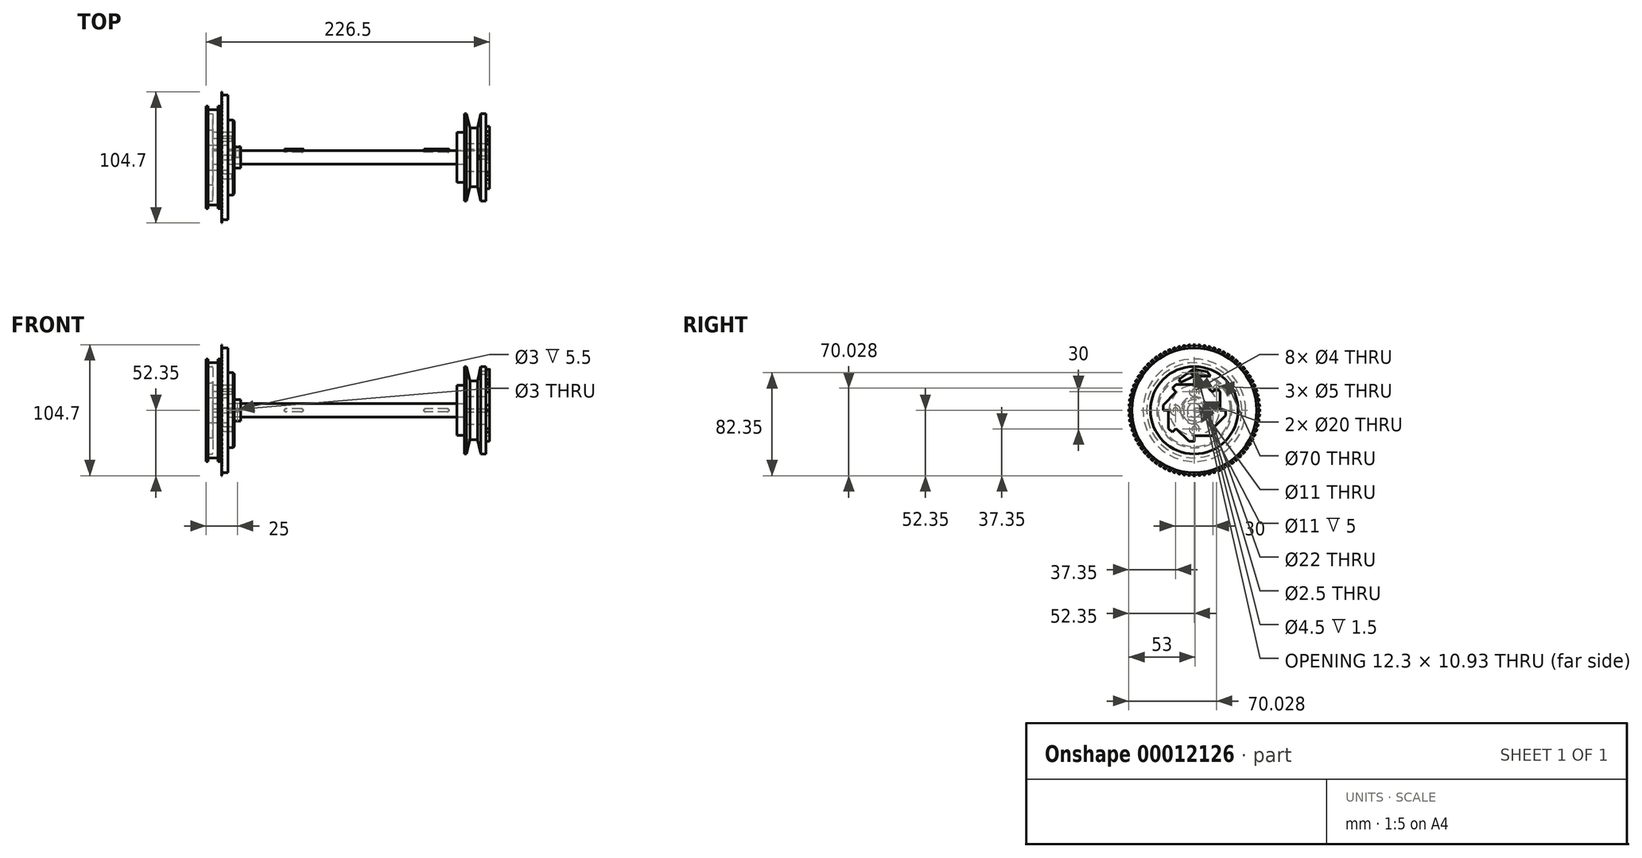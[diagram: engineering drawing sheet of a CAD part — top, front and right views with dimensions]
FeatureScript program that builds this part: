
annotation { "Feature Type Name" : "Feature", "Feature Type Description" : "" }
export const myFeature = defineFeature(function(context is Context, id is Id, definition is map)
    precondition{}
    {
        {
            var Q0;
            Q0=qCreatedBy(makeId("Right.planeOp"),FACE);
            var sketch = newSketch(context, id + "F0", { "sketchPlane" : qUnion([Q0])});
            skCircle(sketch, "E0", {"center": v(0, 0) * mm, "radius": 5.5 * mm});
            skSolve(sketch);
        }
        {
            var Q0;
            Q0=makeQuery(id+"F0.imprint","IMPRINT",FACE,{"disambiguationData":[TD([[makeQuery(id+"F0.imprint","IMPRINT",EDGE,{"derivedFrom":sQuery(id+"F0.wireOp",EDGE,"E0")}),1.0]])]});
            extrude(context, id + "F1", {"entities" : qUnion([Q0]), "depth" : 204 * mm, "symmetric" : true});
        }
        {
            var Q0;
            Q0=qCreatedBy(makeId("Front.planeOp"),FACE);
            cPlane(context, id + "F2", {"entities" : qUnion([Q0]), "cplaneType" : CPlaneType.OFFSET, "offset" : 5.5 * mm, "oppositeDirection" : true, "width" : 150 * mm, "height" : 150 * mm});
        }
        {
            var Q0;
            Q0=qCreatedBy(id+"F2.planeOp",FACE);
            var sketch = newSketch(context, id + "F3", { "sketchPlane" : qUnion([Q0])});
            skLineSegment(sketch, "E1.0", {"start": v(102, 5.5) * mm, "end": v(102, -5.5) * mm});
            skLineSegment(sketch, "E1.1", {"start": v(-102, 5.5) * mm, "end": v(-102, -5.5) * mm});
            skLineSegment(sketch, "E2", {"start": v(102, 0) * mm, "end": v(69.5, 0) * mm, "construction": true});
            skCircle(sketch, "E3", {"center": v(68.25, 0) * mm, "radius": 1.25 * mm});
            skCircle(sketch, "E4", {"center": v(50.75, 0) * mm, "radius": 1.25 * mm});
            skLineSegment(sketch, "E5", {"start": v(68.25, 1.25) * mm, "end": v(50.75, 1.25) * mm});
            skLineSegment(sketch, "E6", {"start": v(68.25, -1.25) * mm, "end": v(50.75, -1.25) * mm});
            skLineSegment(sketch, "E7", {"start": v(-102, 0) * mm, "end": v(-62, 0) * mm, "construction": true});
            skCircle(sketch, "E8", {"center": v(-60.75, 0) * mm, "radius": 1.25 * mm});
            skCircle(sketch, "E9", {"center": v(-48.25, 0) * mm, "radius": 1.25 * mm});
            skLineSegment(sketch, "E10", {"start": v(-48.25, 1.25) * mm, "end": v(-60.75, 1.25) * mm});
            skLineSegment(sketch, "E11", {"start": v(-48.25, -1.25) * mm, "end": v(-60.75, -1.25) * mm});
            skSolve(sketch);
        }
        {
            var Q0;
            {var subQ1=sQuery(id+"F3.wireOp",EDGE,"E5");Q0=makeQuery(id+"F3.imprint","IMPRINT",FACE,{"disambiguationData":[TD([[makeQuery(id+"F3.imprint","IMPRINT",EDGE,{"derivedFrom":subQ1}),1.0]])]});}
            var Q1;
            {var subQ0=sQuery(id+"F3.wireOp",EDGE,"E3");var subQ2=makeQuery(id+"F3.imprint","INTERSECT",VERTEX,{"derivedFrom":[subQ0,sQuery(id+"F3.wireOp",EDGE,"E5")]});Q1=makeQuery(id+"F3.imprint","IMPRINT",FACE,{"disambiguationData":[TD([[makeQuery(id+"F3.imprint","IMPRINT",EDGE,{"disambiguationData":[TD([[subQ2,-1.0]])],"derivedFrom":subQ0}),1.0]])]});}
            var Q2;
            {var subQ0=sQuery(id+"F3.wireOp",EDGE,"E4");var subQ2=makeQuery(id+"F3.imprint","INTERSECT",VERTEX,{"derivedFrom":[subQ0,sQuery(id+"F3.wireOp",EDGE,"E5")]});Q2=makeQuery(id+"F3.imprint","IMPRINT",FACE,{"disambiguationData":[TD([[makeQuery(id+"F3.imprint","IMPRINT",EDGE,{"disambiguationData":[TD([[subQ2,-1.0]])],"derivedFrom":subQ0}),1.0]])]});}
            var Q3;
            {var subQ0=sQuery(id+"F3.wireOp",EDGE,"E9");var subQ2=makeQuery(id+"F3.imprint","INTERSECT",VERTEX,{"derivedFrom":[subQ0,sQuery(id+"F3.wireOp",EDGE,"E10")]});Q3=makeQuery(id+"F3.imprint","IMPRINT",FACE,{"disambiguationData":[TD([[makeQuery(id+"F3.imprint","IMPRINT",EDGE,{"disambiguationData":[TD([[subQ2,-1.0]])],"derivedFrom":subQ0}),1.0]])]});}
            var Q4;
            {var subQ1=sQuery(id+"F3.wireOp",EDGE,"E10");Q4=makeQuery(id+"F3.imprint","IMPRINT",FACE,{"disambiguationData":[TD([[makeQuery(id+"F3.imprint","IMPRINT",EDGE,{"derivedFrom":subQ1}),1.0]])]});}
            var Q5;
            {var subQ0=sQuery(id+"F3.wireOp",EDGE,"E8");var subQ2=makeQuery(id+"F3.imprint","INTERSECT",VERTEX,{"derivedFrom":[subQ0,sQuery(id+"F3.wireOp",EDGE,"E10")]});Q5=makeQuery(id+"F3.imprint","IMPRINT",FACE,{"disambiguationData":[TD([[makeQuery(id+"F3.imprint","IMPRINT",EDGE,{"disambiguationData":[TD([[subQ2,-1.0]])],"derivedFrom":subQ0}),1.0]])]});}
            extrude(context, id + "F4", {"entities" : qUnion([Q0, Q1, Q2, Q3, Q4, Q5]), "operationType" : NewBodyOperationType.REMOVE, "depth" : 1.3 * mm});
        }
        {
            var Q0;
            {var subQ0=sQuery(id+"F3.wireOp",EDGE,"E3");var subQ2=makeQuery(id+"F3.imprint","INTERSECT",VERTEX,{"derivedFrom":[subQ0,sQuery(id+"F3.wireOp",EDGE,"E5")]});Q0=makeQuery(id+"F3.imprint","IMPRINT",FACE,{"disambiguationData":[TD([[makeQuery(id+"F3.imprint","IMPRINT",EDGE,{"disambiguationData":[TD([[subQ2,-1.0]])],"derivedFrom":subQ0}),1.0]])]});}
            var Q1;
            {var subQ1=sQuery(id+"F3.wireOp",EDGE,"E5");Q1=makeQuery(id+"F3.imprint","IMPRINT",FACE,{"disambiguationData":[TD([[makeQuery(id+"F3.imprint","IMPRINT",EDGE,{"derivedFrom":subQ1}),1.0]])]});}
            var Q2;
            {var subQ0=sQuery(id+"F3.wireOp",EDGE,"E4");var subQ2=makeQuery(id+"F3.imprint","INTERSECT",VERTEX,{"derivedFrom":[subQ0,sQuery(id+"F3.wireOp",EDGE,"E5")]});Q2=makeQuery(id+"F3.imprint","IMPRINT",FACE,{"disambiguationData":[TD([[makeQuery(id+"F3.imprint","IMPRINT",EDGE,{"disambiguationData":[TD([[subQ2,-1.0]])],"derivedFrom":subQ0}),1.0]])]});}
            var Q3;
            {var subQ0=sQuery(id+"F3.wireOp",EDGE,"E9");var subQ2=makeQuery(id+"F3.imprint","INTERSECT",VERTEX,{"derivedFrom":[subQ0,sQuery(id+"F3.wireOp",EDGE,"E10")]});Q3=makeQuery(id+"F3.imprint","IMPRINT",FACE,{"disambiguationData":[TD([[makeQuery(id+"F3.imprint","IMPRINT",EDGE,{"disambiguationData":[TD([[subQ2,-1.0]])],"derivedFrom":subQ0}),1.0]])]});}
            var Q4;
            {var subQ1=sQuery(id+"F3.wireOp",EDGE,"E10");Q4=makeQuery(id+"F3.imprint","IMPRINT",FACE,{"disambiguationData":[TD([[makeQuery(id+"F3.imprint","IMPRINT",EDGE,{"derivedFrom":subQ1}),1.0]])]});}
            var Q5;
            {var subQ0=sQuery(id+"F3.wireOp",EDGE,"E8");var subQ2=makeQuery(id+"F3.imprint","INTERSECT",VERTEX,{"derivedFrom":[subQ0,sQuery(id+"F3.wireOp",EDGE,"E10")]});Q5=makeQuery(id+"F3.imprint","IMPRINT",FACE,{"disambiguationData":[TD([[makeQuery(id+"F3.imprint","IMPRINT",EDGE,{"disambiguationData":[TD([[subQ2,-1.0]])],"derivedFrom":subQ0}),1.0]])]});}
            extrude(context, id + "F5", {"entities" : qUnion([Q0, Q1, Q2, Q3, Q4, Q5]), "depth" : 2.5 * mm, "symmetric" : true});
        }
        {
            var Q0;
            Q0=makeQuery(id+"F1.opExtrude","CAP_FACE",FACE,{"disambiguationData":[OSD([sQuery(id+"F0.wireOp",EDGE,"E0")])],"isStart":true});
            var sketch = newSketch(context, id + "F6", { "sketchPlane" : qUnion([Q0])});
            skCircle(sketch, "E12", {"center": v(0, 0) * mm, "radius": 10 * mm});
            skCircle(sketch, "E13", {"center": v(0, 0) * mm, "radius": 30 * mm});
            skLineSegment(sketch, "E14", {"start": v(0, 0) * mm, "end": v(0, -15) * mm, "construction": true});
            skLineSegment(sketch, "E15", {"start": v(0, 0) * mm, "end": v(-17.68, 17.68) * mm, "construction": true});
            skLineSegment(sketch, "E16", {"start": v(0, 0) * mm, "end": v(-5.5, 0) * mm, "construction": true});
            skCircle(sketch, "E17", {"center": v(0, -15) * mm, "radius": 2 * mm});
            skCircle(sketch, "E18", {"center": v(-17.68, 17.68) * mm, "radius": 2.5 * mm});
            skLineSegment(sketch, "E19.rect.bottom", {"start": v(-6.8, -1.25) * mm, "end": v(-4.2, -1.25) * mm});
            skLineSegment(sketch, "E19.rect.top", {"start": v(-6.8, 1.25) * mm, "end": v(-4.2, 1.25) * mm});
            skLineSegment(sketch, "E19.rect.left", {"start": v(-6.8, -1.25) * mm, "end": v(-6.8, 1.25) * mm});
            skLineSegment(sketch, "E19.rect.right", {"start": v(-4.2, -1.25) * mm, "end": v(-4.2, 1.25) * mm});
            skPoint(sketch, "E19.rect.middle", {"position": v(-5.5, 0) * mm});
            skCircle(sketch, "E20.1.0", {"center": v(15, 0) * mm, "radius": 2 * mm});
            skCircle(sketch, "E20.2.0", {"center": v(0, 15) * mm, "radius": 2 * mm});
            skCircle(sketch, "E20.3.0", {"center": v(-15, 0) * mm, "radius": 2 * mm});
            skSolve(sketch);
        }
        {
            var Q0;
            Q0=makeQuery(id+"F6.imprint","IMPRINT",FACE,{"disambiguationData":[TD([[makeQuery(id+"F6.imprint","IMPRINT",EDGE,{"derivedFrom":sQuery(id+"F6.wireOp",EDGE,"E12")}),-1.0]])]});
            extrude(context, id + "F7", {"entities" : qUnion([Q0]), "depth" : 5 * mm});
        }
        {
            var Q0;
            Q0=makeQuery(id+"F6.imprint","IMPRINT",FACE,{"disambiguationData":[TD([[makeQuery(id+"F6.imprint","IMPRINT",EDGE,{"derivedFrom":sQuery(id+"F6.wireOp",EDGE,"E12")}),1.0]])]});
            extrude(context, id + "F8", {"entities" : qUnion([Q0]), "operationType" : NewBodyOperationType.ADD, "depth" : 17 * mm});
        }
        {
            var Q0;
            Q0=makeQuery(id+"F7.opExtrude","CAP_EDGE",EDGE,{"disambiguationData":[OSD([sQuery(id+"F6.wireOp",EDGE,"E13")])],"isStart":true});
            chamfer(context, id + "F9", {"entities" : qUnion([Q0]), "width" : 1 * mm, "tangentPropagation" : true});
        }
        {
            var Q0;
            Q0=makeQuery(id+"F7.opExtrude","CAP_EDGE",EDGE,{"disambiguationData":[OSD([sQuery(id+"F6.wireOp",EDGE,"E20.1.0")])],"isStart":true});
            var Q1;
            Q1=makeQuery(id+"F7.opExtrude","CAP_EDGE",EDGE,{"disambiguationData":[OSD([sQuery(id+"F6.wireOp",EDGE,"E17")])],"isStart":true});
            var Q2;
            Q2=makeQuery(id+"F7.opExtrude","CAP_EDGE",EDGE,{"disambiguationData":[OSD([sQuery(id+"F6.wireOp",EDGE,"E20.3.0")])],"isStart":true});
            var Q3;
            Q3=makeQuery(id+"F7.opExtrude","CAP_EDGE",EDGE,{"disambiguationData":[OSD([sQuery(id+"F6.wireOp",EDGE,"E20.2.0")])],"isStart":true});
            chamfer(context, id + "F10", {"entities" : qUnion([Q0, Q1, Q2, Q3]), "width" : 2 * mm, "tangentPropagation" : true});
        }
        {
            var Q0;
            Q0=makeQuery(id+"F1.opExtrude","CAP_FACE",FACE,{"disambiguationData":[OSD([sQuery(id+"F0.wireOp",EDGE,"E0")])],"isStart":false});
            var sketch = newSketch(context, id + "F11", { "sketchPlane" : qUnion([Q0])});
            skLineSegment(sketch, "E21.0", {"start": v(4.25, 1.25) * mm, "end": v(6.75, 1.25) * mm});
            skLineSegment(sketch, "E21.1", {"start": v(4.25, -1.25) * mm, "end": v(6.75, -1.25) * mm});
            skCircle(sketch, "E22", {"center": v(0, 0) * mm, "radius": 11 * mm});
            skCircle(sketch, "E23", {"center": v(0, 0) * mm, "radius": 20.5 * mm});
            skCircle(sketch, "E24", {"center": v(0, 0) * mm, "radius": 25.25 * mm});
            skLineSegment(sketch, "E25", {"start": v(0, 0) * mm, "end": v(5.5, 0) * mm, "construction": true});
            skLineSegment(sketch, "E26.rect.bottom", {"start": v(6.8, -1.25) * mm, "end": v(4.2, -1.25) * mm});
            skLineSegment(sketch, "E26.rect.top", {"start": v(6.8, 1.25) * mm, "end": v(4.2, 1.25) * mm});
            skLineSegment(sketch, "E26.rect.left", {"start": v(6.8, -1.25) * mm, "end": v(6.8, 1.25) * mm});
            skLineSegment(sketch, "E26.rect.right", {"start": v(4.2, -1.25) * mm, "end": v(4.2, 1.25) * mm});
            skPoint(sketch, "E26.rect.middle", {"position": v(5.5, 0) * mm});
            skLineSegment(sketch, "E27", {"start": v(20.5, 0) * mm, "end": v(25.25, 0) * mm});
            skLineSegment(sketch, "E28.1.0", {"start": v(14.5, 14.5) * mm, "end": v(17.85, 17.85) * mm});
            skLineSegment(sketch, "E28.2.0", {"start": v(0, 20.5) * mm, "end": v(0, 25.25) * mm});
            skLineSegment(sketch, "E28.3.0", {"start": v(-14.5, 14.5) * mm, "end": v(-17.85, 17.85) * mm});
            skLineSegment(sketch, "E28.4.0", {"start": v(-20.5, 0) * mm, "end": v(-25.25, 0) * mm});
            skLineSegment(sketch, "E28.5.0", {"start": v(-14.5, -14.5) * mm, "end": v(-17.85, -17.85) * mm});
            skLineSegment(sketch, "E28.6.0", {"start": v(0, -20.5) * mm, "end": v(0, -25.25) * mm});
            skLineSegment(sketch, "E28.7.0", {"start": v(14.5, -14.5) * mm, "end": v(17.85, -17.85) * mm});
            skLineSegment(sketch, "E29", {"start": v(0, -20.5) * mm, "end": v(14.74, -20.5) * mm});
            skLineSegment(sketch, "E30", {"start": v(14.74, -20.5) * mm, "end": v(17.62, -17.62) * mm});
            skLineSegment(sketch, "E31.1.0", {"start": v(14.5, -14.5) * mm, "end": v(24.92, -4.07) * mm});
            skLineSegment(sketch, "E31.1.1", {"start": v(24.92, -4.07) * mm, "end": v(24.92, 0) * mm});
            skLineSegment(sketch, "E31.2.0", {"start": v(20.5, 0) * mm, "end": v(20.5, 14.74) * mm});
            skLineSegment(sketch, "E31.2.1", {"start": v(20.5, 14.74) * mm, "end": v(17.62, 17.62) * mm});
            skLineSegment(sketch, "E31.3.0", {"start": v(14.5, 14.5) * mm, "end": v(4.07, 24.92) * mm});
            skLineSegment(sketch, "E31.3.1", {"start": v(4.07, 24.92) * mm, "end": v(0, 24.92) * mm});
            skLineSegment(sketch, "E31.4.0", {"start": v(0, 20.5) * mm, "end": v(-14.74, 20.5) * mm});
            skLineSegment(sketch, "E31.4.1", {"start": v(-14.74, 20.5) * mm, "end": v(-17.62, 17.62) * mm});
            skLineSegment(sketch, "E31.5.0", {"start": v(-14.5, 14.5) * mm, "end": v(-24.92, 4.07) * mm});
            skLineSegment(sketch, "E31.5.1", {"start": v(-24.92, 4.07) * mm, "end": v(-24.92, 0) * mm});
            skLineSegment(sketch, "E31.6.0", {"start": v(-20.5, 0) * mm, "end": v(-20.5, -14.74) * mm});
            skLineSegment(sketch, "E31.6.1", {"start": v(-20.5, -14.74) * mm, "end": v(-17.62, -17.62) * mm});
            skLineSegment(sketch, "E31.7.0", {"start": v(-14.5, -14.5) * mm, "end": v(-4.07, -24.92) * mm});
            skLineSegment(sketch, "E31.7.1", {"start": v(-4.07, -24.92) * mm, "end": v(0, -24.92) * mm});
            skSolve(sketch);
        }
        {
            var Q0;
            {var subQ1=sQuery(id+"F11.wireOp",EDGE,"E31.5.0");Q0=makeQuery(id+"F11.imprint","IMPRINT",FACE,{"disambiguationData":[TD([[makeQuery(id+"F11.imprint","IMPRINT",EDGE,{"derivedFrom":subQ1}),1.0]])]});}
            var Q1;
            {var subQ1=sQuery(id+"F11.wireOp",EDGE,"E31.4.0");Q1=makeQuery(id+"F11.imprint","IMPRINT",FACE,{"disambiguationData":[TD([[makeQuery(id+"F11.imprint","IMPRINT",EDGE,{"derivedFrom":subQ1}),1.0]])]});}
            var Q2;
            {var subQ1=sQuery(id+"F11.wireOp",EDGE,"E31.3.0");Q2=makeQuery(id+"F11.imprint","IMPRINT",FACE,{"disambiguationData":[TD([[makeQuery(id+"F11.imprint","IMPRINT",EDGE,{"derivedFrom":subQ1}),1.0]])]});}
            var Q3;
            {var subQ1=sQuery(id+"F11.wireOp",EDGE,"E31.2.0");Q3=makeQuery(id+"F11.imprint","IMPRINT",FACE,{"disambiguationData":[TD([[makeQuery(id+"F11.imprint","IMPRINT",EDGE,{"derivedFrom":subQ1}),1.0]])]});}
            var Q4;
            {var subQ1=sQuery(id+"F11.wireOp",EDGE,"E31.1.0");Q4=makeQuery(id+"F11.imprint","IMPRINT",FACE,{"disambiguationData":[TD([[makeQuery(id+"F11.imprint","IMPRINT",EDGE,{"derivedFrom":subQ1}),1.0]])]});}
            var Q5;
            {var subQ1=sQuery(id+"F11.wireOp",EDGE,"E29");Q5=makeQuery(id+"F11.imprint","IMPRINT",FACE,{"disambiguationData":[TD([[makeQuery(id+"F11.imprint","IMPRINT",EDGE,{"derivedFrom":subQ1}),1.0]])]});}
            var Q6;
            {var subQ1=sQuery(id+"F11.wireOp",EDGE,"E31.7.0");Q6=makeQuery(id+"F11.imprint","IMPRINT",FACE,{"disambiguationData":[TD([[makeQuery(id+"F11.imprint","IMPRINT",EDGE,{"derivedFrom":subQ1}),1.0]])]});}
            var Q7;
            {var subQ1=sQuery(id+"F11.wireOp",EDGE,"E31.6.0");Q7=makeQuery(id+"F11.imprint","IMPRINT",FACE,{"disambiguationData":[TD([[makeQuery(id+"F11.imprint","IMPRINT",EDGE,{"derivedFrom":subQ1}),1.0]])]});}
            var Q8;
            Q8=makeQuery(id+"F11.imprint","IMPRINT",FACE,{"disambiguationData":[TD([[makeQuery(id+"F11.imprint","IMPRINT",EDGE,{"derivedFrom":sQuery(id+"F11.wireOp",EDGE,"E22")}),-1.0]])]});
            extrude(context, id + "F12", {"entities" : qUnion([Q0, Q1, Q2, Q3, Q4, Q5, Q6, Q7, Q8]), "oppositeDirection" : true, "depth" : 3 * mm});
        }
        {
            var Q0;
            Q0=makeQuery(id+"F11.imprint","IMPRINT",FACE,{"disambiguationData":[TD([[makeQuery(id+"F11.imprint","IMPRINT",EDGE,{"derivedFrom":sQuery(id+"F11.wireOp",EDGE,"E22")}),1.0]])]});
            extrude(context, id + "F13", {"entities" : qUnion([Q0]), "operationType" : NewBodyOperationType.ADD, "oppositeDirection" : true, "depth" : 20 * mm});
        }
        {
            var Q0;
            Q0=makeQuery(id+"F7.opExtrude","CAP_FACE",FACE,{"disambiguationData":[OSD([sQuery(id+"F6.wireOp",EDGE,"E12"),sQuery(id+"F6.wireOp",EDGE,"E13"),sQuery(id+"F6.wireOp",EDGE,"E17"),sQuery(id+"F6.wireOp",EDGE,"E18"),sQuery(id+"F6.wireOp",EDGE,"E20.1.0"),sQuery(id+"F6.wireOp",EDGE,"E20.2.0"),sQuery(id+"F6.wireOp",EDGE,"E20.3.0")])],"isStart":false});
            var sketch = newSketch(context, id + "F14", { "sketchPlane" : qUnion([Q0])});
            skCircle(sketch, "E32", {"center": v(0, 0) * mm, "radius": 52.35 * mm});
            skCircle(sketch, "E33", {"center": v(0, 0) * mm, "radius": 51.1 * mm, "construction": true});
            skCircle(sketch, "E34", {"center": v(0, 0) * mm, "radius": 49.85 * mm});
            skLineSegment(sketch, "E35", {"start": v(0, 0) * mm, "end": v(0, 52.35) * mm, "construction": true});
            skLineSegment(sketch, "E36", {"start": v(0, 49.85) * mm, "end": v(15, 49.85) * mm, "construction": true});
            skLineSegment(sketch, "E37", {"start": v(0, 0) * mm, "end": v(-1, 51.1) * mm, "construction": true});
            skLineSegment(sketch, "E38", {"start": v(0, 0) * mm, "end": v(-3.15, 49.75) * mm, "construction": true});
            skArc(sketch, "E39", {"start": v(-0.86, 52.34) * mm, "mid": v(-1, 51.1) * mm, "end": v(-1.05, 49.84) * mm});
            skArc(sketch, "E40.0.MirrorCS", {"start": v(0.86, 52.34) * mm, "mid": v(1, 51.1) * mm, "end": v(1.05, 49.84) * mm});
            skSolve(sketch);
        }
        {
            var Q0;
            Q0=makeQuery(id+"F14.imprint","IMPRINT",FACE,{"disambiguationData":[TD([[makeQuery(id+"F14.imprint","IMPRINT",EDGE,{"derivedFrom":makeQuery(id+"F7.opExtrude","CAP_EDGE",EDGE,{"disambiguationData":[OSD([sQuery(id+"F6.wireOp",EDGE,"E13")])],"isStart":false})}),-1.0]])]});
            var Q1;
            {var subQ1=sQuery(id+"F14.wireOp",EDGE,"E39");Q1=makeQuery(id+"F14.imprint","IMPRINT",FACE,{"disambiguationData":[TD([[makeQuery(id+"F14.imprint","IMPRINT",EDGE,{"derivedFrom":subQ1}),1.0]])]});}
            var Q2;
            Q2=makeQuery(id+"F14.imprint","IMPRINT",FACE,{"disambiguationData":[TD([[makeQuery(id+"F14.imprint","IMPRINT",EDGE,{"derivedFrom":makeQuery(id+"F7.opExtrude","CAP_EDGE",EDGE,{"disambiguationData":[OSD([sQuery(id+"F6.wireOp",EDGE,"E13")])],"isStart":false})}),1.0]])]});
            extrude(context, id + "F15", {"entities" : qUnion([Q0, Q1, Q2]), "depth" : 5 * mm});
        }
        {
            var Q0;
            Q0=makeQuery(id+"F15.opExtrude","SWEPT_FACE",FACE,{"disambiguationData":[OSD([sQuery(id+"F14.wireOp",EDGE,"E40.0.MirrorCS")])]});
            var Q1;
            Q1=makeQuery(id+"F15.opExtrude","SWEPT_FACE",FACE,{"disambiguationData":[OSD([sQuery(id+"F14.wireOp",EDGE,"E32")])]});
            var Q2;
            Q2=makeQuery(id+"F15.opExtrude","SWEPT_FACE",FACE,{"disambiguationData":[OSD([sQuery(id+"F14.wireOp",EDGE,"E39")])]});
            var Q3;
            Q3=makeQuery(id+"F8.opExtrude","CAP_EDGE",EDGE,{"disambiguationData":[OSD([sQuery(id+"F6.wireOp",EDGE,"E12")])],"isStart":false});
            circularPattern(context, id + "F16", {"faces" : qUnion([Q0, Q1, Q2]), "axis" : qUnion([Q3]), "angle" : 4.5 * degree, "instanceCount" : round(80), "patternType" : PatternType.FACE, "computeTransformsWithoutBuiltin" : true});
        }
        {
            var Q0;
            Q0=qCreatedBy(makeId("Front.planeOp"),FACE);
            var sketch = newSketch(context, id + "F17", { "sketchPlane" : qUnion([Q0])});
            skLineSegment(sketch, "E41.0", {"start": v(-107, -30) * mm, "end": v(-107, 30) * mm});
            skLineSegment(sketch, "E42", {"start": v(-107, 0) * mm, "end": v(-134.37, 0) * mm, "construction": true});
            skLineSegment(sketch, "E43", {"start": v(-107, 0) * mm, "end": v(-107, 49.85) * mm, "construction": true});
            skLineSegment(sketch, "E44.bottom", {"start": v(-107, 49.85) * mm, "end": v(-112, 49.85) * mm});
            skLineSegment(sketch, "E44.top", {"start": v(-107, 52.35) * mm, "end": v(-112, 52.35) * mm});
            skLineSegment(sketch, "E44.left", {"start": v(-107, 49.85) * mm, "end": v(-107, 52.35) * mm});
            skLineSegment(sketch, "E44.right", {"start": v(-112, 49.85) * mm, "end": v(-112, 52.35) * mm});
            skLineSegment(sketch, "E45", {"start": v(-109.5, 52.35) * mm, "end": v(-109.5, 49.85) * mm, "construction": true});
            skLineSegment(sketch, "E46", {"start": v(-107, 49.85) * mm, "end": v(-117, 49.85) * mm, "construction": true});
            skLineSegment(sketch, "E47", {"start": v(-107, 51.1) * mm, "end": v(-112, 51.1) * mm, "construction": true});
            skArc(sketch, "E48", {"start": v(-107, 51.1) * mm, "mid": v(-107.1, 51.73) * mm, "end": v(-107.24, 52.35) * mm});
            skArc(sketch, "E49.0.MirrorCS", {"start": v(-112, 51.1) * mm, "mid": v(-111.9, 51.73) * mm, "end": v(-111.76, 52.35) * mm});
            skSolve(sketch);
        }
        {
            var Q0;
            {var subQ0=sQuery(id+"F17.wireOp",EDGE,"E49.0.MirrorCS");Q0=makeQuery(id+"F17.imprint","IMPRINT",FACE,{"disambiguationData":[TD([[makeQuery(id+"F17.imprint","IMPRINT",EDGE,{"derivedFrom":subQ0}),1.0]])]});}
            var Q1;
            {var subQ0=sQuery(id+"F17.wireOp",EDGE,"E48");Q1=makeQuery(id+"F17.imprint","IMPRINT",FACE,{"disambiguationData":[TD([[makeQuery(id+"F17.imprint","IMPRINT",EDGE,{"derivedFrom":subQ0}),-1.0]])]});}
            var Q2;
            Q2=sQuery(id+"F17.wireOp",EDGE,"E42");
            revolve(context, id + "F18", {"operationType" : NewBodyOperationType.REMOVE, "entities" : qUnion([Q0, Q1]), "axis" : qUnion([Q2]), "revolveType" : RevolveType.FULL, "oppositeDirection" : true});
        }
        {
            var Q0;
            Q0=qCreatedBy(makeId("Front.planeOp"),FACE);
            var sketch = newSketch(context, id + "F19", { "sketchPlane" : qUnion([Q0])});
            skLineSegment(sketch, "E50.0", {"start": v(-112, -10) * mm, "end": v(-112, 10) * mm});
            skLineSegment(sketch, "E51", {"start": v(-112, 0) * mm, "end": v(-131.3, 0) * mm, "construction": true});
            skLineSegment(sketch, "E52", {"start": v(-112, 10) * mm, "end": v(-112, 22) * mm});
            skLineSegment(sketch, "E53", {"start": v(-112, 22) * mm, "end": v(-113.5, 22) * mm});
            skLineSegment(sketch, "E54", {"start": v(-113.5, 22) * mm, "end": v(-113.5, 41) * mm});
            skLineSegment(sketch, "E55", {"start": v(-113.5, 41) * mm, "end": v(-115, 41) * mm});
            skLineSegment(sketch, "E56", {"start": v(-115, 41) * mm, "end": v(-115, 38) * mm});
            skLineSegment(sketch, "E57", {"start": v(-115, 38) * mm, "end": v(-123, 38) * mm});
            skLineSegment(sketch, "E58", {"start": v(-123, 38) * mm, "end": v(-123, 41) * mm});
            skLineSegment(sketch, "E59", {"start": v(-123, 41) * mm, "end": v(-124.5, 41) * mm});
            skLineSegment(sketch, "E60", {"start": v(-124.5, 41) * mm, "end": v(-124.5, 35) * mm});
            skLineSegment(sketch, "E61", {"start": v(-124.5, 35) * mm, "end": v(-119, 35) * mm});
            skLineSegment(sketch, "E62", {"start": v(-119, 35) * mm, "end": v(-119, 22) * mm});
            skLineSegment(sketch, "E63", {"start": v(-119, 22) * mm, "end": v(-124.5, 22) * mm});
            skLineSegment(sketch, "E64", {"start": v(-124.5, 22) * mm, "end": v(-124.5, 10) * mm});
            skLineSegment(sketch, "E65", {"start": v(-124.5, 10) * mm, "end": v(-112, 10) * mm});
            skSolve(sketch);
        }
        {
            var Q0;
            Q0=makeQuery(id+"F19.imprint","IMPRINT",FACE,{"disambiguationData":[TD([[makeQuery(id+"F19.imprint","IMPRINT",EDGE,{"derivedFrom":sQuery(id+"F19.wireOp",EDGE,"E52")}),1.0]])]});
            var Q1;
            Q1=sQuery(id+"F19.wireOp",EDGE,"E51");
            revolve(context, id + "F20", {"entities" : qUnion([Q0]), "axis" : qUnion([Q1]), "revolveType" : RevolveType.FULL});
        }
        {
            var Q0;
            Q0=makeQuery(id+"F20.opRevolve","SWEPT_EDGE",EDGE,{"disambiguationData":[OSD([sQuery(id+"F19.wireOp",EDGE,"E53"),sQuery(id+"F19.wireOp",EDGE,"E54")])]});
            var Q1;
            Q1=makeQuery(id+"F20.opRevolve","SWEPT_EDGE",EDGE,{"disambiguationData":[OSD([sQuery(id+"F19.wireOp",EDGE,"E62"),sQuery(id+"F19.wireOp",EDGE,"E63")])]});
            var Q2;
            Q2=makeQuery(id+"F20.opRevolve","SWEPT_EDGE",EDGE,{"disambiguationData":[OSD([sQuery(id+"F19.wireOp",EDGE,"E61"),sQuery(id+"F19.wireOp",EDGE,"E62")])]});
            var Q3;
            Q3=makeQuery(id+"F20.opRevolve","SWEPT_EDGE",EDGE,{"disambiguationData":[OSD([sQuery(id+"F19.wireOp",EDGE,"E63"),sQuery(id+"F19.wireOp",EDGE,"E64")])]});
            var Q4;
            Q4=makeQuery(id+"F20.opRevolve","SWEPT_EDGE",EDGE,{"disambiguationData":[OSD([sQuery(id+"F19.wireOp",EDGE,"E60"),sQuery(id+"F19.wireOp",EDGE,"E61")])]});
            fillet(context, id + "F21", {"entities" : qUnion([Q0, Q1, Q2, Q3, Q4]), "radius" : 1 * mm, "tangentPropagation" : true, "allowEdgeOverflow" : false});
        }
        {
            var Q0;
            Q0=makeQuery(id+"F20.opRevolve","SWEPT_FACE",FACE,{"disambiguationData":[OSD([sQuery(id+"F19.wireOp",EDGE,"E54")])]});
            var sketch = newSketch(context, id + "F22", { "sketchPlane" : qUnion([Q0])});
            skCircle(sketch, "E66.0", {"center": v(17.68, 17.68) * mm, "radius": 2.5 * mm});
            skSolve(sketch);
        }
        {
            var Q0;
            {var subQ0=sQuery(id+"F19.wireOp",EDGE,"E54");var subQ1=makeQuery(id+"F21.opFillet","BLEND_EDGE",EDGE,{"blendedFrom":[makeQuery(id+"F20.opRevolve","SWEPT_EDGE",EDGE,{"disambiguationData":[OSD([sQuery(id+"F19.wireOp",EDGE,"E53"),subQ0])]}),makeQuery(id+"F20.opRevolve","SWEPT_FACE",FACE,{"disambiguationData":[OSD([subQ0])]})],"blendedInto":[makeQuery(id+"F20.opRevolve","SWEPT_FACE",FACE,{"disambiguationData":[OSD([subQ0])]})]});var subQ2=sQuery(id+"F22.wireOp",EDGE,"E66.0");var subQ4=makeQuery(id+"F22.imprint","INTERSECT",VERTEX,{"disambiguationData":[OD(0.0)],"derivedFrom":[subQ1,subQ2]});Q0=makeQuery(id+"F22.imprint","IMPRINT",FACE,{"disambiguationData":[TD([[makeQuery(id+"F22.imprint","IMPRINT",EDGE,{"disambiguationData":[TD([[subQ4,1.0]])],"derivedFrom":subQ2}),1.0]])]});}
            var Q1;
            {var subQ0=sQuery(id+"F19.wireOp",EDGE,"E54");var subQ1=makeQuery(id+"F21.opFillet","BLEND_EDGE",EDGE,{"blendedFrom":[makeQuery(id+"F20.opRevolve","SWEPT_EDGE",EDGE,{"disambiguationData":[OSD([sQuery(id+"F19.wireOp",EDGE,"E53"),subQ0])]}),makeQuery(id+"F20.opRevolve","SWEPT_FACE",FACE,{"disambiguationData":[OSD([subQ0])]})],"blendedInto":[makeQuery(id+"F20.opRevolve","SWEPT_FACE",FACE,{"disambiguationData":[OSD([subQ0])]})]});var subQ2=sQuery(id+"F22.wireOp",EDGE,"E66.0");var subQ4=makeQuery(id+"F22.imprint","INTERSECT",VERTEX,{"disambiguationData":[OD(0.0)],"derivedFrom":[subQ1,subQ2]});Q1=makeQuery(id+"F22.imprint","IMPRINT",FACE,{"disambiguationData":[TD([[makeQuery(id+"F22.imprint","IMPRINT",EDGE,{"disambiguationData":[TD([[subQ4,-1.0]])],"derivedFrom":subQ2}),1.0]])]});}
            extrude(context, id + "F23", {"entities" : qUnion([Q0, Q1]), "operationType" : NewBodyOperationType.REMOVE, "oppositeDirection" : true, "depth" : 13 * mm, "symmetric" : true});
        }
        {
            var Q0;
            Q0=qCreatedBy(makeId("Front.planeOp"),FACE);
            var sketch = newSketch(context, id + "F24", { "sketchPlane" : qUnion([Q0])});
            skLineSegment(sketch, "E67.0", {"start": v(82, 11) * mm, "end": v(82, -11) * mm});
            skLineSegment(sketch, "E67.1", {"start": v(99, 11) * mm, "end": v(99, -11) * mm});
            skLineSegment(sketch, "E68", {"start": v(99, 0) * mm, "end": v(82, 0) * mm, "construction": true});
            skLineSegment(sketch, "E69", {"start": v(99, 11) * mm, "end": v(99, 35) * mm});
            skLineSegment(sketch, "E70", {"start": v(99, 35) * mm, "end": v(95, 35) * mm});
            skLineSegment(sketch, "E71", {"start": v(95, 35) * mm, "end": v(92.25, 23.5) * mm});
            skLineSegment(sketch, "E72", {"start": v(92.25, 23.5) * mm, "end": v(86.25, 23.5) * mm});
            skLineSegment(sketch, "E73", {"start": v(86.25, 23.5) * mm, "end": v(83.5, 35) * mm});
            skLineSegment(sketch, "E74", {"start": v(83.5, 35) * mm, "end": v(82, 35) * mm});
            skLineSegment(sketch, "E75", {"start": v(82, 35) * mm, "end": v(82, 11) * mm});
            skLineSegment(sketch, "E76", {"start": v(82, 11) * mm, "end": v(99, 11) * mm});
            skSolve(sketch);
        }
        {
            var Q0;
            Q0=makeQuery(id+"F24.imprint","IMPRINT",FACE,{"disambiguationData":[TD([[makeQuery(id+"F24.imprint","IMPRINT",EDGE,{"derivedFrom":sQuery(id+"F24.wireOp",EDGE,"E69")}),1.0]])]});
            var Q1;
            Q1=sQuery(id+"F24.wireOp",EDGE,"E68");
            revolve(context, id + "F25", {"entities" : qUnion([Q0]), "axis" : qUnion([Q1]), "revolveType" : RevolveType.FULL});
        }
        {
            var Q0;
            Q0=makeQuery(id+"F25.opRevolve","SWEPT_FACE",FACE,{"disambiguationData":[OSD([sQuery(id+"F24.wireOp",EDGE,"E69")])]});
            var sketch = newSketch(context, id + "F26", { "sketchPlane" : qUnion([Q0])});
            skLineSegment(sketch, "E77", {"start": v(0, 0) * mm, "end": v(0, 30) * mm, "construction": true});
            skCircle(sketch, "E78", {"center": v(0, 30) * mm, "radius": 1.25 * mm});
            skSolve(sketch);
        }
        {
            var Q0;
            Q0=makeQuery(id+"F26.imprint","IMPRINT",FACE,{"disambiguationData":[TD([[makeQuery(id+"F26.imprint","IMPRINT",EDGE,{"derivedFrom":sQuery(id+"F26.wireOp",EDGE,"E78")}),1.0]])]});
            extrude(context, id + "F27", {"entities" : qUnion([Q0]), "operationType" : NewBodyOperationType.REMOVE, "oppositeDirection" : true, "depth" : 8 * mm});
        }
        {
            var Q0;
            Q0=makeQuery(id+"F25.opRevolve","SWEPT_FACE",FACE,{"disambiguationData":[OSD([sQuery(id+"F24.wireOp",EDGE,"E75")])]});
            var sketch = newSketch(context, id + "F28", { "sketchPlane" : qUnion([Q0])});
            skCircle(sketch, "E79.0", {"center": v(0, 0) * mm, "radius": 23.5 * mm});
            skLineSegment(sketch, "E80", {"start": v(0, 0) * mm, "end": v(0, -23.5) * mm, "construction": true});
            skCircle(sketch, "E81", {"center": v(0, -24.25) * mm, "radius": 0.75 * mm});
            skSolve(sketch);
        }
        {
            var Q0;
            Q0=makeQuery(id+"F28.imprint","IMPRINT",FACE,{"disambiguationData":[TD([[makeQuery(id+"F28.imprint","IMPRINT",EDGE,{"derivedFrom":sQuery(id+"F28.wireOp",EDGE,"E81")}),1.0]])]});
            extrude(context, id + "F29", {"entities" : qUnion([Q0]), "operationType" : NewBodyOperationType.REMOVE, "oppositeDirection" : true, "depth" : 8 * mm});
        }
        {
            var Q0;
            Q0=makeQuery(id+"F13.opExtrude","CAP_FACE",FACE,{"disambiguationData":[OSD([sQuery(id+"F0.wireOp",EDGE,"E0"),sQuery(id+"F11.wireOp",EDGE,"E22"),sQuery(id+"F11.wireOp",EDGE,"E26.rect.bottom"),sQuery(id+"F11.wireOp",EDGE,"E26.rect.top"),sQuery(id+"F11.wireOp",EDGE,"E26.rect.left")])],"isStart":false});
            var sketch = newSketch(context, id + "F30", { "sketchPlane" : qUnion([Q0])});
            skCircle(sketch, "E82.0", {"center": v(0, 0) * mm, "radius": 5.5 * mm});
            skCircle(sketch, "E83", {"center": v(0, 0) * mm, "radius": 20 * mm});
            skSolve(sketch);
        }
        {
            var Q0;
            Q0=makeQuery(id+"F30.imprint","IMPRINT",FACE,{"disambiguationData":[TD([[makeQuery(id+"F30.imprint","IMPRINT",EDGE,{"derivedFrom":sQuery(id+"F30.wireOp",EDGE,"E83")}),1.0]])]});
            var Q1;
            Q1=makeQuery(id+"F30.imprint","IMPRINT",FACE,{"disambiguationData":[TD([[makeQuery(id+"F30.imprint","IMPRINT",EDGE,{"disambiguationData":[OD(0.0)],"derivedFrom":sQuery(id+"F30.wireOp",EDGE,"E82.0")}),1.0]])]});
            var Q2;
            Q2=makeQuery(id+"F30.imprint","IMPRINT",FACE,{"disambiguationData":[TD([[makeQuery(id+"F30.imprint","IMPRINT",EDGE,{"disambiguationData":[OD(1.0)],"derivedFrom":sQuery(id+"F30.wireOp",EDGE,"E82.0")}),-1.0]])]});
            extrude(context, id + "F31", {"entities" : qUnion([Q0, Q1, Q2]), "depth" : 6 * mm});
        }
        {
            var Q0;
            {var subQ0=sQuery(id+"F6.wireOp",EDGE,"E12");Q0=makeQuery(id+"F8.boolean.opBoolean","MERGE",FACE,{"derivedFrom":[makeQuery(id+"F7.opExtrude","CAP_FACE",FACE,{"disambiguationData":[OSD([subQ0,sQuery(id+"F6.wireOp",EDGE,"E13"),sQuery(id+"F6.wireOp",EDGE,"E17"),sQuery(id+"F6.wireOp",EDGE,"E18"),sQuery(id+"F6.wireOp",EDGE,"E20.1.0"),sQuery(id+"F6.wireOp",EDGE,"E20.2.0"),sQuery(id+"F6.wireOp",EDGE,"E20.3.0")])],"isStart":true}),makeQuery(id+"F8.opExtrude","CAP_FACE",FACE,{"disambiguationData":[OSD([sQuery(id+"F0.wireOp",EDGE,"E0"),subQ0,sQuery(id+"F6.wireOp",EDGE,"E19.rect.bottom"),sQuery(id+"F6.wireOp",EDGE,"E19.rect.top"),sQuery(id+"F6.wireOp",EDGE,"E19.rect.left")])],"isStart":true})]});}
            var sketch = newSketch(context, id + "F32", { "sketchPlane" : qUnion([Q0])});
            skCircle(sketch, "E84.0", {"center": v(0, 0) * mm, "radius": 5.5 * mm});
            skCircle(sketch, "E85", {"center": v(0, 0) * mm, "radius": 8.5 * mm});
            skSolve(sketch);
        }
        {
            var Q0;
            Q0=makeQuery(id+"F25.opRevolve","SWEPT_FACE",FACE,{"disambiguationData":[OSD([sQuery(id+"F24.wireOp",EDGE,"E69")])]});
            var sketch = newSketch(context, id + "F33", { "sketchPlane" : qUnion([Q0])});
            skCircle(sketch, "E86.0", {"center": v(0, 30) * mm, "radius": 1.25 * mm});
            skLineSegment(sketch, "E87", {"start": v(0, 27.25) * mm, "end": v(13, 27.25) * mm});
            skLineSegment(sketch, "E88", {"start": v(13, 27.25) * mm, "end": v(10.5, 30.75) * mm});
            skLineSegment(sketch, "E89", {"start": v(10.5, 30.75) * mm, "end": v(-0.63, 32.93) * mm});
            skLineSegment(sketch, "E90", {"start": v(-0.63, 32.93) * mm, "end": v(-12.2, 24.7) * mm});
            skLineSegment(sketch, "E91", {"start": v(-12.2, 24.7) * mm, "end": v(-11, 22.25) * mm});
            skLineSegment(sketch, "E92", {"start": v(-11, 22.25) * mm, "end": v(0, 27.25) * mm});
            skCircle(sketch, "E93", {"center": v(0, 30) * mm, "radius": 2.25 * mm});
            skCircle(sketch, "E94", {"center": v(0, 30) * mm, "radius": 2.75 * mm});
            skSolve(sketch);
        }
        {
            var Q0;
            Q0=makeQuery(id+"F32.imprint","IMPRINT",FACE,{"disambiguationData":[TD([[makeQuery(id+"F32.imprint","IMPRINT",EDGE,{"derivedFrom":sQuery(id+"F32.wireOp",EDGE,"E85")}),1.0]])]});
            var Q1;
            {var subQ1=makeQuery(id+"F8.opExtrude","CAP_EDGE",EDGE,{"disambiguationData":[OSD([sQuery(id+"F6.wireOp",EDGE,"E19.rect.bottom")])],"isStart":true});Q1=makeQuery(id+"F32.imprint","IMPRINT",FACE,{"disambiguationData":[TD([[makeQuery(id+"F32.imprint","IMPRINT",EDGE,{"derivedFrom":subQ1}),-1.0]])]});}
            extrude(context, id + "F34", {"entities" : qUnion([Q0, Q1]), "depth" : 5 * mm});
        }
        {
            var Q0;
            Q0=qCreatedBy(makeId("Front.planeOp"),FACE);
            var sketch = newSketch(context, id + "F35", { "sketchPlane" : qUnion([Q0])});
            skLineSegment(sketch, "E95.0", {"start": v(-97, 8.5) * mm, "end": v(-97, -8.5) * mm});
            skLineSegment(sketch, "E95.1", {"start": v(-102, 8.5) * mm, "end": v(-102, -8.5) * mm});
            skLineSegment(sketch, "E96", {"start": v(-97, 0) * mm, "end": v(-102, 0) * mm, "construction": true});
            skCircle(sketch, "E97", {"center": v(-99.5, 0) * mm, "radius": 1.5 * mm});
            skSolve(sketch);
        }
        {
            var Q0;
            Q0=makeQuery(id+"F35.imprint","IMPRINT",FACE,{"disambiguationData":[TD([[makeQuery(id+"F35.imprint","IMPRINT",EDGE,{"derivedFrom":sQuery(id+"F35.wireOp",EDGE,"E97")}),1.0]])]});
            extrude(context, id + "F36", {"entities" : qUnion([Q0]), "operationType" : NewBodyOperationType.REMOVE, "oppositeDirection" : true, "depth" : 8.5 * mm});
        }
        {
            var Q0;
            {var subQ4=sQuery(id+"F33.wireOp",EDGE,"E91");Q0=makeQuery(id+"F33.imprint","IMPRINT",FACE,{"disambiguationData":[TD([[makeQuery(id+"F33.imprint","IMPRINT",EDGE,{"derivedFrom":subQ4}),1.0]])]});}
            var Q1;
            Q1=makeQuery(id+"F33.imprint","IMPRINT",FACE,{"disambiguationData":[TD([[makeQuery(id+"F33.imprint","IMPRINT",EDGE,{"derivedFrom":sQuery(id+"F33.wireOp",EDGE,"E93")}),-1.0]])]});
            var Q2;
            {var subQ3=sQuery(id+"F33.wireOp",EDGE,"E87");Q2=makeQuery(id+"F33.imprint","IMPRINT",FACE,{"disambiguationData":[TD([[makeQuery(id+"F33.imprint","IMPRINT",EDGE,{"derivedFrom":subQ3}),1.0]])]});}
            extrude(context, id + "F37", {"entities" : qUnion([Q0, Q1, Q2]), "depth" : 3 * mm});
        }
        {
            var Q0;
            Q0=makeQuery(id+"F33.imprint","IMPRINT",FACE,{"disambiguationData":[TD([[makeQuery(id+"F33.imprint","IMPRINT",EDGE,{"derivedFrom":sQuery(id+"F33.wireOp",EDGE,"E86.0")}),-1.0]])]});
            extrude(context, id + "F38", {"entities" : qUnion([Q0]), "operationType" : NewBodyOperationType.ADD, "depth" : 1.5 * mm});
        }
    });
